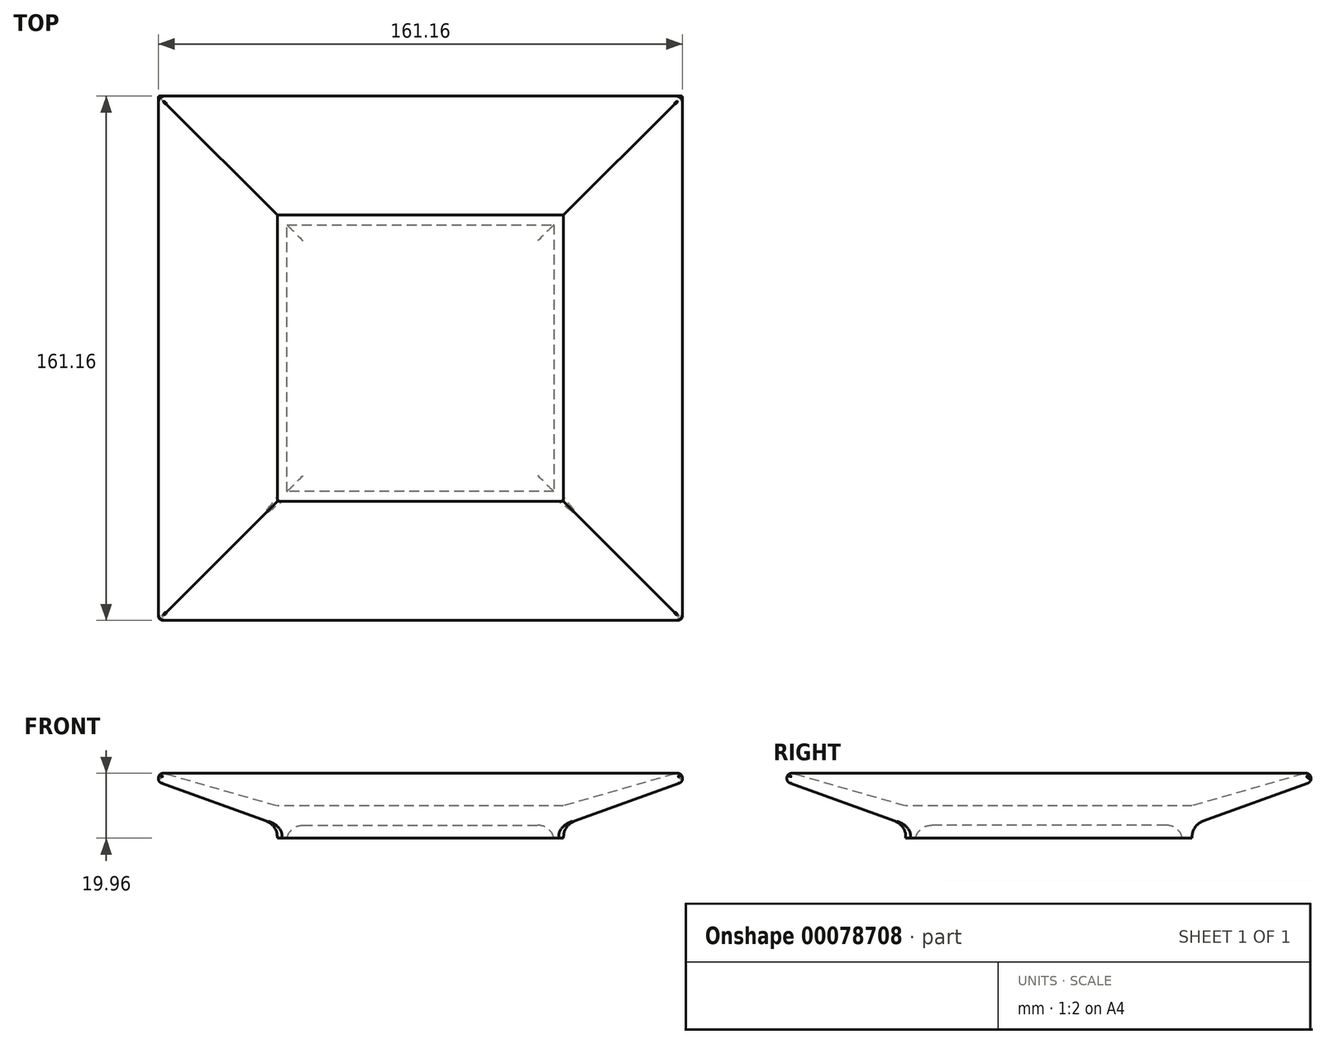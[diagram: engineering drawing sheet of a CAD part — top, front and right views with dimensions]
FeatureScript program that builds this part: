
annotation { "Feature Type Name" : "Feature", "Feature Type Description" : "" }
export const myFeature = defineFeature(function(context is Context, id is Id, definition is map)
    precondition{}
    {
        {
            var Q0;
            Q0=qCreatedBy(makeId("Top.planeOp"),FACE);
            var sketch = newSketch(context, id + "F0", { "sketchPlane" : qUnion([Q0])});
            skLineSegment(sketch, "E0.bottom", {"start": v(44, 44) * mm, "end": v(-44, 44) * mm});
            skLineSegment(sketch, "E0.top", {"start": v(44, -44) * mm, "end": v(-44, -44) * mm});
            skLineSegment(sketch, "E0.left", {"start": v(44, 44) * mm, "end": v(44, -44) * mm});
            skLineSegment(sketch, "E0.right", {"start": v(-44, 44) * mm, "end": v(-44, -44) * mm});
            skPoint(sketch, "E0.middle", {"position": v(0, 0) * mm});
            skSolve(sketch);
        }
        {
            var Q0;
            Q0=makeQuery(id+"F0.imprint","IMPRINT",FACE,{"disambiguationData":[TD([[makeQuery(id+"F0.imprint","IMPRINT",EDGE,{"derivedFrom":sQuery(id+"F0.wireOp",EDGE,"E0.bottom")}),1.0]])]});
            extrude(context, id + "F1", {"entities" : qUnion([Q0]), "depth" : 6 * mm});
        }
        {
            var Q0;
            Q0=qCreatedBy(makeId("Front.planeOp"),FACE);
            var sketch = newSketch(context, id + "F2", { "sketchPlane" : qUnion([Q0])});
            skLineSegment(sketch, "E1.0", {"start": v(44, 6) * mm, "end": v(44, 0) * mm});
            skLineSegment(sketch, "E2", {"start": v(44, 0) * mm, "end": v(81, 0) * mm, "construction": true});
            skLineSegment(sketch, "E3", {"start": v(44, 0) * mm, "end": v(81, 13.47) * mm});
            skLineSegment(sketch, "E4", {"start": v(81, 13.47) * mm, "end": v(79.97, 16.29) * mm});
            skLineSegment(sketch, "E5", {"start": v(79.97, 16.29) * mm, "end": v(44, 6) * mm});
            skLineSegment(sketch, "E6", {"start": v(0, 58.89) * mm, "end": v(0, -59.83) * mm});
            skSolve(sketch);
        }
        {
            var Q0;
            Q0=makeQuery(id+"F2.imprint","IMPRINT",FACE,{"disambiguationData":[TD([[makeQuery(id+"F2.imprint","IMPRINT",EDGE,{"derivedFrom":sQuery(id+"F2.wireOp",EDGE,"E1.0")}),1.0]])]});
            extrude(context, id + "F3", {"entities" : qUnion([Q0]), "endBound" : BoundingType.SYMMETRIC, "depth" : 165.54 * mm});
        }
        {
            var Q0;
            Q0=makeQuery(id+"F3.opExtrude","SWEPT_BODY",BODY,{"disambiguationData":[OSD([sQuery(id+"F2.wireOp",EDGE,"E1.0"),sQuery(id+"F2.wireOp",EDGE,"E3"),sQuery(id+"F2.wireOp",EDGE,"E4"),sQuery(id+"F2.wireOp",EDGE,"E5")])]});
            var Q1;
            Q1=sQuery(id+"F2.wireOp",EDGE,"E6");
            circularPattern(context, id + "F4", {"operationType" : NewBodyOperationType.ADD, "entities" : qUnion([Q0]), "axis" : qUnion([Q1]), "angle" : 360 * degree, "instanceCount" : 4, "equalSpace" : true});
        }
        {
            var Q0;
            Q0=qCreatedBy(makeId("Front.planeOp"),FACE);
            var sketch = newSketch(context, id + "F5", { "sketchPlane" : qUnion([Q0])});
            skLineSegment(sketch, "E7.0", {"start": v(44, 0) * mm, "end": v(81, 13.47) * mm});
            skLineSegment(sketch, "E8.0", {"start": v(81, 13.47) * mm, "end": v(79.97, 16.29) * mm});
            skLineSegment(sketch, "E9", {"start": v(79.97, 16.29) * mm, "end": v(88.12, 25.8) * mm});
            skLineSegment(sketch, "E10", {"start": v(88.12, 25.8) * mm, "end": v(101.77, -20) * mm});
            skLineSegment(sketch, "E11", {"start": v(101.77, -20) * mm, "end": v(44.92, -15.49) * mm});
            skLineSegment(sketch, "E12", {"start": v(44.92, -15.49) * mm, "end": v(44, 0) * mm});
            skSolve(sketch);
        }
        {
            var Q0;
            Q0=makeQuery(id+"F5.imprint","IMPRINT",FACE,{"disambiguationData":[TD([[makeQuery(id+"F5.imprint","IMPRINT",EDGE,{"derivedFrom":sQuery(id+"F5.wireOp",EDGE,"E7.0")}),-1.0]])]});
            extrude(context, id + "F6", {"entities" : qUnion([Q0]), "endBound" : BoundingType.SYMMETRIC, "depth" : 220.76 * mm});
        }
        {
            var Q0;
            Q0=makeQuery(id+"F6.opExtrude","SWEPT_BODY",BODY,{"disambiguationData":[OSD([sQuery(id+"F5.wireOp",EDGE,"E7.0"),sQuery(id+"F5.wireOp",EDGE,"E8.0"),sQuery(id+"F5.wireOp",EDGE,"E9"),sQuery(id+"F5.wireOp",EDGE,"E10"),sQuery(id+"F5.wireOp",EDGE,"E11"),sQuery(id+"F5.wireOp",EDGE,"E12")])]});
            var Q1;
            Q1=sQuery(id+"F2.wireOp",EDGE,"E6");
            circularPattern(context, id + "F7", {"operationType" : NewBodyOperationType.REMOVE, "entities" : qUnion([Q0]), "axis" : qUnion([Q1]), "angle" : 360 * degree, "instanceCount" : 4, "equalSpace" : true});
        }
        {
            var Q0;
            Q0=makeQuery(id+"F1.opExtrude","CAP_FACE",FACE,{"disambiguationData":[OSD([sQuery(id+"F0.wireOp",EDGE,"E0.bottom"),sQuery(id+"F0.wireOp",EDGE,"E0.top"),sQuery(id+"F0.wireOp",EDGE,"E0.left"),sQuery(id+"F0.wireOp",EDGE,"E0.right")])],"isStart":true});
            var sketch = newSketch(context, id + "F8", { "sketchPlane" : qUnion([Q0])});
            skLineSegment(sketch, "E13.0.0", {"start": v(-44, -44) * mm, "end": v(44, -44) * mm});
            skLineSegment(sketch, "E13.0.2", {"start": v(44, -44) * mm, "end": v(44, 44) * mm});
            skLineSegment(sketch, "E13.0.4", {"start": v(44, 44) * mm, "end": v(-44, 44) * mm});
            skLineSegment(sketch, "E13.0.6", {"start": v(-44, 44) * mm, "end": v(-44, -44) * mm});
            skLineSegment(sketch, "E14.0", {"start": v(-41, -41) * mm, "end": v(41, -41) * mm});
            skLineSegment(sketch, "E14.1", {"start": v(-41, 41) * mm, "end": v(-41, -41) * mm});
            skLineSegment(sketch, "E14.2", {"start": v(41, 41) * mm, "end": v(-41, 41) * mm});
            skLineSegment(sketch, "E14.3", {"start": v(41, -41) * mm, "end": v(41, 41) * mm});
            skPoint(sketch, "E15.orphan", {"position": v(44, 43.49) * mm});
            skPoint(sketch, "E16.orphan", {"position": v(-43.49, 44) * mm});
            skPoint(sketch, "E17.orphan", {"position": v(-44, -43.49) * mm});
            skPoint(sketch, "E18.orphan", {"position": v(-43.49, -44) * mm});
            skPoint(sketch, "E19.orphan", {"position": v(-44, -45.08) * mm});
            skPoint(sketch, "E20.orphan", {"position": v(43.49, -44) * mm});
            skPoint(sketch, "E21.orphan", {"position": v(45.17, -44) * mm});
            skSolve(sketch);
        }
        {
            var Q0;
            Q0=makeQuery(id+"F8.imprint","IMPRINT",FACE,{"disambiguationData":[TD([[makeQuery(id+"F8.imprint","IMPRINT",EDGE,{"derivedFrom":sQuery(id+"F8.wireOp",EDGE,"E13.0.0")}),-1.0]])]});
            extrude(context, id + "F9", {"entities" : qUnion([Q0]), "operationType" : NewBodyOperationType.ADD, "depth" : 4 * mm});
        }
        {
            var Q0;
            {var subQ0=sQuery(id+"F2.wireOp",EDGE,"E5");var subQ1=makeQuery(id+"F3.opExtrude","SWEPT_FACE",FACE,{"disambiguationData":[OSD([subQ0])]});var subQ2=sQuery(id+"F2.wireOp",EDGE,"E4");var subQ3=makeQuery(id+"F3.opExtrude","SWEPT_FACE",FACE,{"disambiguationData":[OSD([subQ2])]});Q0=makeQuery(id+"F4.boolean.opBoolean","SPLIT",EDGE,{"disambiguationData":[TD([subQ3,subQ1,makeQuery(id+"F4.opPattern","COPY",FACE,{"derivedFrom":subQ3,"instanceName":"1"}),makeQuery(id+"F4.opPattern","COPY",FACE,{"derivedFrom":subQ1,"instanceName":"1"}),makeQuery(id+"F4.opPattern","COPY",FACE,{"derivedFrom":subQ3,"instanceName":"2"}),makeQuery(id+"F4.opPattern","COPY",FACE,{"derivedFrom":subQ1,"instanceName":"2"})])],"derivedFrom":makeQuery(id+"F4.opPattern","COPY",EDGE,{"derivedFrom":makeQuery(id+"F3.opExtrude","SWEPT_EDGE",EDGE,{"disambiguationData":[OSD([subQ2,subQ0])]}),"instanceName":"1"})});}
            var Q1;
            {var subQ0=sQuery(id+"F2.wireOp",EDGE,"E5");var subQ1=makeQuery(id+"F3.opExtrude","SWEPT_FACE",FACE,{"disambiguationData":[OSD([subQ0])]});var subQ2=sQuery(id+"F2.wireOp",EDGE,"E4");var subQ3=makeQuery(id+"F3.opExtrude","SWEPT_FACE",FACE,{"disambiguationData":[OSD([subQ2])]});Q1=makeQuery(id+"F4.boolean.opBoolean","SPLIT",EDGE,{"disambiguationData":[TD([makeQuery(id+"F4.opPattern","COPY",FACE,{"derivedFrom":subQ3,"instanceName":"1"}),makeQuery(id+"F4.opPattern","COPY",FACE,{"derivedFrom":subQ1,"instanceName":"1"}),makeQuery(id+"F4.opPattern","COPY",FACE,{"derivedFrom":subQ3,"instanceName":"2"}),makeQuery(id+"F4.opPattern","COPY",FACE,{"derivedFrom":subQ1,"instanceName":"2"}),makeQuery(id+"F4.opPattern","COPY",FACE,{"derivedFrom":subQ3,"instanceName":"3"}),makeQuery(id+"F4.opPattern","COPY",FACE,{"derivedFrom":subQ1,"instanceName":"3"})])],"derivedFrom":makeQuery(id+"F4.opPattern","COPY",EDGE,{"derivedFrom":makeQuery(id+"F3.opExtrude","SWEPT_EDGE",EDGE,{"disambiguationData":[OSD([subQ2,subQ0])]}),"instanceName":"2"})});}
            var Q2;
            {var subQ0=sQuery(id+"F2.wireOp",EDGE,"E5");var subQ1=makeQuery(id+"F3.opExtrude","SWEPT_FACE",FACE,{"disambiguationData":[OSD([subQ0])]});var subQ2=sQuery(id+"F2.wireOp",EDGE,"E4");var subQ3=makeQuery(id+"F3.opExtrude","SWEPT_FACE",FACE,{"disambiguationData":[OSD([subQ2])]});Q2=makeQuery(id+"F4.boolean.opBoolean","SPLIT",EDGE,{"disambiguationData":[TD([subQ3,subQ1,makeQuery(id+"F4.opPattern","COPY",FACE,{"derivedFrom":subQ3,"instanceName":"2"}),makeQuery(id+"F4.opPattern","COPY",FACE,{"derivedFrom":subQ1,"instanceName":"2"}),makeQuery(id+"F4.opPattern","COPY",FACE,{"derivedFrom":subQ3,"instanceName":"3"}),makeQuery(id+"F4.opPattern","COPY",FACE,{"derivedFrom":subQ1,"instanceName":"3"})])],"derivedFrom":makeQuery(id+"F4.opPattern","COPY",EDGE,{"derivedFrom":makeQuery(id+"F3.opExtrude","SWEPT_EDGE",EDGE,{"disambiguationData":[OSD([subQ2,subQ0])]}),"instanceName":"3"})});}
            var Q3;
            {var subQ0=sQuery(id+"F2.wireOp",EDGE,"E5");var subQ1=makeQuery(id+"F3.opExtrude","SWEPT_FACE",FACE,{"disambiguationData":[OSD([subQ0])]});var subQ2=sQuery(id+"F2.wireOp",EDGE,"E4");var subQ3=makeQuery(id+"F3.opExtrude","SWEPT_FACE",FACE,{"disambiguationData":[OSD([subQ2])]});Q3=makeQuery(id+"F4.boolean.opBoolean","SPLIT",EDGE,{"disambiguationData":[TD([subQ3,subQ1,makeQuery(id+"F4.opPattern","COPY",FACE,{"derivedFrom":subQ3,"instanceName":"1"}),makeQuery(id+"F4.opPattern","COPY",FACE,{"derivedFrom":subQ1,"instanceName":"1"}),makeQuery(id+"F4.opPattern","COPY",FACE,{"derivedFrom":subQ3,"instanceName":"3"}),makeQuery(id+"F4.opPattern","COPY",FACE,{"derivedFrom":subQ1,"instanceName":"3"})])],"derivedFrom":makeQuery(id+"F3.opExtrude","SWEPT_EDGE",EDGE,{"disambiguationData":[OSD([subQ2,subQ0])]})});}
            var Q4;
            {var subQ0=makeQuery(id+"F3.opExtrude","SWEPT_FACE",FACE,{"disambiguationData":[OSD([sQuery(id+"F2.wireOp",EDGE,"E5")])]});var subQ1=sQuery(id+"F2.wireOp",EDGE,"E3");var subQ2=sQuery(id+"F2.wireOp",EDGE,"E4");Q4=makeQuery(id+"F7.boolean.opBoolean","MERGE",EDGE,{"derivedFrom":[makeQuery(id+"F4.boolean.opBoolean","SPLIT",EDGE,{"disambiguationData":[TD([makeQuery(id+"F4.opPattern","COPY",FACE,{"derivedFrom":subQ0,"instanceName":"1"})])],"derivedFrom":makeQuery(id+"F4.opPattern","COPY",EDGE,{"derivedFrom":makeQuery(id+"F3.opExtrude","SWEPT_EDGE",EDGE,{"disambiguationData":[OSD([subQ1,subQ2])]}),"instanceName":"2"})}),makeQuery(id+"F7.opPattern","COPY",EDGE,{"derivedFrom":makeQuery(id+"F6.opExtrude","SWEPT_EDGE",EDGE,{"disambiguationData":[OSD([sQuery(id+"F5.wireOp",EDGE,"E7.0"),sQuery(id+"F5.wireOp",EDGE,"E8.0")])]}),"instanceName":"2"})]});}
            var Q5;
            {var subQ0=makeQuery(id+"F3.opExtrude","SWEPT_FACE",FACE,{"disambiguationData":[OSD([sQuery(id+"F2.wireOp",EDGE,"E5")])]});var subQ1=sQuery(id+"F2.wireOp",EDGE,"E3");var subQ2=sQuery(id+"F2.wireOp",EDGE,"E4");Q5=makeQuery(id+"F7.boolean.opBoolean","MERGE",EDGE,{"derivedFrom":[makeQuery(id+"F4.boolean.opBoolean","SPLIT",EDGE,{"disambiguationData":[TD([subQ0])],"derivedFrom":makeQuery(id+"F4.opPattern","COPY",EDGE,{"derivedFrom":makeQuery(id+"F3.opExtrude","SWEPT_EDGE",EDGE,{"disambiguationData":[OSD([subQ1,subQ2])]}),"instanceName":"1"})}),makeQuery(id+"F7.opPattern","COPY",EDGE,{"derivedFrom":makeQuery(id+"F6.opExtrude","SWEPT_EDGE",EDGE,{"disambiguationData":[OSD([sQuery(id+"F5.wireOp",EDGE,"E7.0"),sQuery(id+"F5.wireOp",EDGE,"E8.0")])]}),"instanceName":"1"})]});}
            var Q6;
            {var subQ0=sQuery(id+"F2.wireOp",EDGE,"E3");var subQ1=sQuery(id+"F2.wireOp",EDGE,"E4");var subQ2=makeQuery(id+"F3.opExtrude","SWEPT_FACE",FACE,{"disambiguationData":[OSD([sQuery(id+"F2.wireOp",EDGE,"E5")])]});Q6=makeQuery(id+"F7.boolean.opBoolean","MERGE",EDGE,{"derivedFrom":[makeQuery(id+"F4.boolean.opBoolean","SPLIT",EDGE,{"disambiguationData":[TD([makeQuery(id+"F4.opPattern","COPY",FACE,{"derivedFrom":subQ2,"instanceName":"1"})])],"derivedFrom":makeQuery(id+"F3.opExtrude","SWEPT_EDGE",EDGE,{"disambiguationData":[OSD([subQ0,subQ1])]})}),makeQuery(id+"F6.opExtrude","SWEPT_EDGE",EDGE,{"disambiguationData":[OSD([sQuery(id+"F5.wireOp",EDGE,"E7.0"),sQuery(id+"F5.wireOp",EDGE,"E8.0")])]})]});}
            var Q7;
            {var subQ0=makeQuery(id+"F3.opExtrude","SWEPT_FACE",FACE,{"disambiguationData":[OSD([sQuery(id+"F2.wireOp",EDGE,"E5")])]});var subQ1=sQuery(id+"F2.wireOp",EDGE,"E3");var subQ2=sQuery(id+"F2.wireOp",EDGE,"E4");Q7=makeQuery(id+"F7.boolean.opBoolean","MERGE",EDGE,{"derivedFrom":[makeQuery(id+"F4.boolean.opBoolean","SPLIT",EDGE,{"disambiguationData":[TD([subQ0])],"derivedFrom":makeQuery(id+"F4.opPattern","COPY",EDGE,{"derivedFrom":makeQuery(id+"F3.opExtrude","SWEPT_EDGE",EDGE,{"disambiguationData":[OSD([subQ1,subQ2])]}),"instanceName":"3"})}),makeQuery(id+"F7.opPattern","COPY",EDGE,{"derivedFrom":makeQuery(id+"F6.opExtrude","SWEPT_EDGE",EDGE,{"disambiguationData":[OSD([sQuery(id+"F5.wireOp",EDGE,"E7.0"),sQuery(id+"F5.wireOp",EDGE,"E8.0")])]}),"instanceName":"3"})]});}
            fillet(context, id + "F10", {"entities" : qUnion([Q0, Q1, Q2, Q3, Q4, Q5, Q6, Q7]), "radius" : 1.5 * mm, "tangentPropagation" : true, "allowEdgeOverflow" : false});
        }
        {
            var Q0;
            Q0=makeQuery(id+"F1.opExtrude","CAP_FACE",FACE,{"disambiguationData":[OSD([sQuery(id+"F0.wireOp",EDGE,"E0.bottom"),sQuery(id+"F0.wireOp",EDGE,"E0.top"),sQuery(id+"F0.wireOp",EDGE,"E0.left"),sQuery(id+"F0.wireOp",EDGE,"E0.right")])],"isStart":true});
            var Q1;
            Q1=makeQuery(id+"F9.boolean.opBoolean","MERGE",EDGE,{"derivedFrom":[makeQuery(id+"F4.boolean.opBoolean","MERGE",EDGE,{"derivedFrom":[makeQuery(id+"F1.opExtrude","CAP_EDGE",EDGE,{"disambiguationData":[OSD([sQuery(id+"F0.wireOp",EDGE,"E0.left")])],"isStart":true}),makeQuery(id+"F3.opExtrude","SWEPT_EDGE",EDGE,{"disambiguationData":[OSD([sQuery(id+"F2.wireOp",EDGE,"E1.0"),sQuery(id+"F2.wireOp",EDGE,"E3")])]})]}),makeQuery(id+"F9.opExtrude","CAP_EDGE",EDGE,{"disambiguationData":[OSD([sQuery(id+"F8.wireOp",EDGE,"E13.0.2")])],"isStart":true})]});
            var Q2;
            Q2=makeQuery(id+"F9.boolean.opBoolean","MERGE",EDGE,{"derivedFrom":[makeQuery(id+"F4.boolean.opBoolean","MERGE",EDGE,{"derivedFrom":[makeQuery(id+"F1.opExtrude","CAP_EDGE",EDGE,{"disambiguationData":[OSD([sQuery(id+"F0.wireOp",EDGE,"E0.top")])],"isStart":true}),makeQuery(id+"F4.opPattern","COPY",EDGE,{"derivedFrom":makeQuery(id+"F3.opExtrude","SWEPT_EDGE",EDGE,{"disambiguationData":[OSD([sQuery(id+"F2.wireOp",EDGE,"E1.0"),sQuery(id+"F2.wireOp",EDGE,"E3")])]}),"instanceName":"1"})]}),makeQuery(id+"F9.opExtrude","CAP_EDGE",EDGE,{"disambiguationData":[OSD([sQuery(id+"F8.wireOp",EDGE,"E13.0.4")])],"isStart":true})]});
            var Q3;
            Q3=makeQuery(id+"F9.boolean.opBoolean","MERGE",EDGE,{"derivedFrom":[makeQuery(id+"F4.boolean.opBoolean","MERGE",EDGE,{"derivedFrom":[makeQuery(id+"F1.opExtrude","CAP_EDGE",EDGE,{"disambiguationData":[OSD([sQuery(id+"F0.wireOp",EDGE,"E0.right")])],"isStart":true}),makeQuery(id+"F4.opPattern","COPY",EDGE,{"derivedFrom":makeQuery(id+"F3.opExtrude","SWEPT_EDGE",EDGE,{"disambiguationData":[OSD([sQuery(id+"F2.wireOp",EDGE,"E1.0"),sQuery(id+"F2.wireOp",EDGE,"E3")])]}),"instanceName":"2"})]}),makeQuery(id+"F9.opExtrude","CAP_EDGE",EDGE,{"disambiguationData":[OSD([sQuery(id+"F8.wireOp",EDGE,"E13.0.6")])],"isStart":true})]});
            var Q4;
            Q4=makeQuery(id+"F9.boolean.opBoolean","MERGE",EDGE,{"derivedFrom":[makeQuery(id+"F4.boolean.opBoolean","MERGE",EDGE,{"derivedFrom":[makeQuery(id+"F1.opExtrude","CAP_EDGE",EDGE,{"disambiguationData":[OSD([sQuery(id+"F0.wireOp",EDGE,"E0.bottom")])],"isStart":true}),makeQuery(id+"F4.opPattern","COPY",EDGE,{"derivedFrom":makeQuery(id+"F3.opExtrude","SWEPT_EDGE",EDGE,{"disambiguationData":[OSD([sQuery(id+"F2.wireOp",EDGE,"E1.0"),sQuery(id+"F2.wireOp",EDGE,"E3")])]}),"instanceName":"3"})]}),makeQuery(id+"F9.opExtrude","CAP_EDGE",EDGE,{"disambiguationData":[OSD([sQuery(id+"F8.wireOp",EDGE,"E13.0.0")])],"isStart":true})]});
            fillet(context, id + "F11", {"entities" : qUnion([Q0, Q1, Q2, Q3, Q4]), "radius" : 5 * mm, "tangentPropagation" : true, "allowEdgeOverflow" : false});
        }
        {
            var Q0;
            {var subQ0=makeQuery(id+"F6.opExtrude","SWEPT_EDGE",EDGE,{"disambiguationData":[OSD([sQuery(id+"F5.wireOp",EDGE,"E7.0"),sQuery(id+"F5.wireOp",EDGE,"E8.0")])]});var subQ1=makeQuery(id+"F3.opExtrude","SWEPT_FACE",FACE,{"disambiguationData":[OSD([sQuery(id+"F2.wireOp",EDGE,"E5")])]});var subQ2=sQuery(id+"F2.wireOp",EDGE,"E3");var subQ4=sQuery(id+"F2.wireOp",EDGE,"E4");var subQ6=makeQuery(id+"F3.opExtrude","SWEPT_EDGE",EDGE,{"disambiguationData":[OSD([subQ2,subQ4])]});Q0=makeQuery(id+"F10.opFillet","BLEND_EDGE",EDGE,{"blendedFrom":[makeQuery(id+"F7.boolean.opBoolean","MERGE",EDGE,{"derivedFrom":[makeQuery(id+"F4.boolean.opBoolean","SPLIT",EDGE,{"disambiguationData":[TD([subQ1])],"derivedFrom":makeQuery(id+"F4.opPattern","COPY",EDGE,{"derivedFrom":subQ6,"instanceName":"1"})}),makeQuery(id+"F7.opPattern","COPY",EDGE,{"derivedFrom":subQ0,"instanceName":"1"})]}),makeQuery(id+"F7.boolean.opBoolean","MERGE",EDGE,{"derivedFrom":[makeQuery(id+"F4.boolean.opBoolean","SPLIT",EDGE,{"disambiguationData":[TD([makeQuery(id+"F4.opPattern","COPY",FACE,{"derivedFrom":subQ1,"instanceName":"1"})])],"derivedFrom":makeQuery(id+"F4.opPattern","COPY",EDGE,{"derivedFrom":subQ6,"instanceName":"2"})}),makeQuery(id+"F7.opPattern","COPY",EDGE,{"derivedFrom":subQ0,"instanceName":"2"})]})],"blendedInto":[]});}
            var Q1;
            {var subQ0=sQuery(id+"F2.wireOp",EDGE,"E5");var subQ1=makeQuery(id+"F3.opExtrude","SWEPT_FACE",FACE,{"disambiguationData":[OSD([subQ0])]});var subQ2=makeQuery(id+"F4.opPattern","COPY",FACE,{"derivedFrom":subQ1,"instanceName":"2"});var subQ3=sQuery(id+"F2.wireOp",EDGE,"E4");var subQ4=makeQuery(id+"F3.opExtrude","SWEPT_FACE",FACE,{"disambiguationData":[OSD([subQ3])]});var subQ5=makeQuery(id+"F4.opPattern","COPY",FACE,{"derivedFrom":subQ4,"instanceName":"2"});var subQ6=makeQuery(id+"F4.opPattern","COPY",FACE,{"derivedFrom":subQ1,"instanceName":"1"});var subQ7=makeQuery(id+"F4.opPattern","COPY",FACE,{"derivedFrom":subQ4,"instanceName":"1"});var subQ8=makeQuery(id+"F3.opExtrude","SWEPT_EDGE",EDGE,{"disambiguationData":[OSD([subQ3,subQ0])]});Q1=makeQuery(id+"F10.opFillet","BLEND_EDGE",EDGE,{"blendedFrom":[makeQuery(id+"F4.boolean.opBoolean","SPLIT",EDGE,{"disambiguationData":[TD([subQ4,subQ1,subQ7,subQ6,subQ5,subQ2])],"derivedFrom":makeQuery(id+"F4.opPattern","COPY",EDGE,{"derivedFrom":subQ8,"instanceName":"1"})}),makeQuery(id+"F4.boolean.opBoolean","SPLIT",EDGE,{"disambiguationData":[TD([subQ7,subQ6,subQ5,subQ2,makeQuery(id+"F4.opPattern","COPY",FACE,{"derivedFrom":subQ4,"instanceName":"3"}),makeQuery(id+"F4.opPattern","COPY",FACE,{"derivedFrom":subQ1,"instanceName":"3"})])],"derivedFrom":makeQuery(id+"F4.opPattern","COPY",EDGE,{"derivedFrom":subQ8,"instanceName":"2"})})],"blendedInto":[]});}
            var Q2;
            {var subQ0=makeQuery(id+"F6.opExtrude","SWEPT_EDGE",EDGE,{"disambiguationData":[OSD([sQuery(id+"F5.wireOp",EDGE,"E7.0"),sQuery(id+"F5.wireOp",EDGE,"E8.0")])]});var subQ1=makeQuery(id+"F3.opExtrude","SWEPT_FACE",FACE,{"disambiguationData":[OSD([sQuery(id+"F2.wireOp",EDGE,"E5")])]});var subQ2=sQuery(id+"F2.wireOp",EDGE,"E3");var subQ4=sQuery(id+"F2.wireOp",EDGE,"E4");var subQ6=makeQuery(id+"F3.opExtrude","SWEPT_EDGE",EDGE,{"disambiguationData":[OSD([subQ2,subQ4])]});Q2=makeQuery(id+"F10.opFillet","BLEND_EDGE",EDGE,{"blendedFrom":[makeQuery(id+"F7.boolean.opBoolean","MERGE",EDGE,{"derivedFrom":[makeQuery(id+"F4.boolean.opBoolean","SPLIT",EDGE,{"disambiguationData":[TD([makeQuery(id+"F4.opPattern","COPY",FACE,{"derivedFrom":subQ1,"instanceName":"1"})])],"derivedFrom":subQ6}),subQ0]}),makeQuery(id+"F7.boolean.opBoolean","MERGE",EDGE,{"derivedFrom":[makeQuery(id+"F4.boolean.opBoolean","SPLIT",EDGE,{"disambiguationData":[TD([subQ1])],"derivedFrom":makeQuery(id+"F4.opPattern","COPY",EDGE,{"derivedFrom":subQ6,"instanceName":"1"})}),makeQuery(id+"F7.opPattern","COPY",EDGE,{"derivedFrom":subQ0,"instanceName":"1"})]})],"blendedInto":[]});}
            var Q3;
            {var subQ0=sQuery(id+"F2.wireOp",EDGE,"E5");var subQ1=makeQuery(id+"F3.opExtrude","SWEPT_FACE",FACE,{"disambiguationData":[OSD([subQ0])]});var subQ2=makeQuery(id+"F4.opPattern","COPY",FACE,{"derivedFrom":subQ1,"instanceName":"1"});var subQ3=sQuery(id+"F2.wireOp",EDGE,"E4");var subQ4=makeQuery(id+"F3.opExtrude","SWEPT_FACE",FACE,{"disambiguationData":[OSD([subQ3])]});var subQ5=makeQuery(id+"F4.opPattern","COPY",FACE,{"derivedFrom":subQ4,"instanceName":"1"});var subQ6=makeQuery(id+"F3.opExtrude","SWEPT_EDGE",EDGE,{"disambiguationData":[OSD([subQ3,subQ0])]});Q3=makeQuery(id+"F10.opFillet","BLEND_EDGE",EDGE,{"blendedFrom":[makeQuery(id+"F4.boolean.opBoolean","SPLIT",EDGE,{"disambiguationData":[TD([subQ4,subQ1,subQ5,subQ2,makeQuery(id+"F4.opPattern","COPY",FACE,{"derivedFrom":subQ4,"instanceName":"3"}),makeQuery(id+"F4.opPattern","COPY",FACE,{"derivedFrom":subQ1,"instanceName":"3"})])],"derivedFrom":subQ6}),makeQuery(id+"F4.boolean.opBoolean","SPLIT",EDGE,{"disambiguationData":[TD([subQ4,subQ1,subQ5,subQ2,makeQuery(id+"F4.opPattern","COPY",FACE,{"derivedFrom":subQ4,"instanceName":"2"}),makeQuery(id+"F4.opPattern","COPY",FACE,{"derivedFrom":subQ1,"instanceName":"2"})])],"derivedFrom":makeQuery(id+"F4.opPattern","COPY",EDGE,{"derivedFrom":subQ6,"instanceName":"1"})})],"blendedInto":[]});}
            var Q4;
            {var subQ0=sQuery(id+"F2.wireOp",EDGE,"E5");var subQ1=makeQuery(id+"F3.opExtrude","SWEPT_FACE",FACE,{"disambiguationData":[OSD([subQ0])]});var subQ2=sQuery(id+"F2.wireOp",EDGE,"E4");var subQ3=makeQuery(id+"F3.opExtrude","SWEPT_FACE",FACE,{"disambiguationData":[OSD([subQ2])]});var subQ4=makeQuery(id+"F4.opPattern","COPY",FACE,{"derivedFrom":subQ3,"instanceName":"3"});var subQ5=makeQuery(id+"F4.opPattern","COPY",FACE,{"derivedFrom":subQ1,"instanceName":"3"});var subQ6=makeQuery(id+"F3.opExtrude","SWEPT_EDGE",EDGE,{"disambiguationData":[OSD([subQ2,subQ0])]});Q4=makeQuery(id+"F10.opFillet","BLEND_EDGE",EDGE,{"blendedFrom":[makeQuery(id+"F4.boolean.opBoolean","SPLIT",EDGE,{"disambiguationData":[TD([subQ3,subQ1,makeQuery(id+"F4.opPattern","COPY",FACE,{"derivedFrom":subQ3,"instanceName":"1"}),makeQuery(id+"F4.opPattern","COPY",FACE,{"derivedFrom":subQ1,"instanceName":"1"}),subQ4,subQ5])],"derivedFrom":subQ6}),makeQuery(id+"F4.boolean.opBoolean","SPLIT",EDGE,{"disambiguationData":[TD([subQ3,subQ1,makeQuery(id+"F4.opPattern","COPY",FACE,{"derivedFrom":subQ3,"instanceName":"2"}),makeQuery(id+"F4.opPattern","COPY",FACE,{"derivedFrom":subQ1,"instanceName":"2"}),subQ4,subQ5])],"derivedFrom":makeQuery(id+"F4.opPattern","COPY",EDGE,{"derivedFrom":subQ6,"instanceName":"3"})})],"blendedInto":[]});}
            var Q5;
            {var subQ0=sQuery(id+"F2.wireOp",EDGE,"E5");var subQ1=makeQuery(id+"F3.opExtrude","SWEPT_FACE",FACE,{"disambiguationData":[OSD([subQ0])]});var subQ2=makeQuery(id+"F4.opPattern","COPY",FACE,{"derivedFrom":subQ1,"instanceName":"2"});var subQ3=sQuery(id+"F2.wireOp",EDGE,"E4");var subQ4=makeQuery(id+"F3.opExtrude","SWEPT_FACE",FACE,{"disambiguationData":[OSD([subQ3])]});var subQ5=makeQuery(id+"F4.opPattern","COPY",FACE,{"derivedFrom":subQ4,"instanceName":"3"});var subQ6=makeQuery(id+"F4.opPattern","COPY",FACE,{"derivedFrom":subQ4,"instanceName":"2"});var subQ7=makeQuery(id+"F4.opPattern","COPY",FACE,{"derivedFrom":subQ1,"instanceName":"3"});var subQ8=makeQuery(id+"F3.opExtrude","SWEPT_EDGE",EDGE,{"disambiguationData":[OSD([subQ3,subQ0])]});Q5=makeQuery(id+"F10.opFillet","BLEND_EDGE",EDGE,{"blendedFrom":[makeQuery(id+"F4.boolean.opBoolean","SPLIT",EDGE,{"disambiguationData":[TD([makeQuery(id+"F4.opPattern","COPY",FACE,{"derivedFrom":subQ4,"instanceName":"1"}),makeQuery(id+"F4.opPattern","COPY",FACE,{"derivedFrom":subQ1,"instanceName":"1"}),subQ6,subQ2,subQ5,subQ7])],"derivedFrom":makeQuery(id+"F4.opPattern","COPY",EDGE,{"derivedFrom":subQ8,"instanceName":"2"})}),makeQuery(id+"F4.boolean.opBoolean","SPLIT",EDGE,{"disambiguationData":[TD([subQ4,subQ1,subQ6,subQ2,subQ5,subQ7])],"derivedFrom":makeQuery(id+"F4.opPattern","COPY",EDGE,{"derivedFrom":subQ8,"instanceName":"3"})})],"blendedInto":[]});}
            fillet(context, id + "F12", {"entities" : qUnion([Q0, Q1, Q2, Q3, Q4, Q5]), "radius" : 1.5 * mm, "tangentPropagation" : true, "allowEdgeOverflow" : false});
        }
    });
